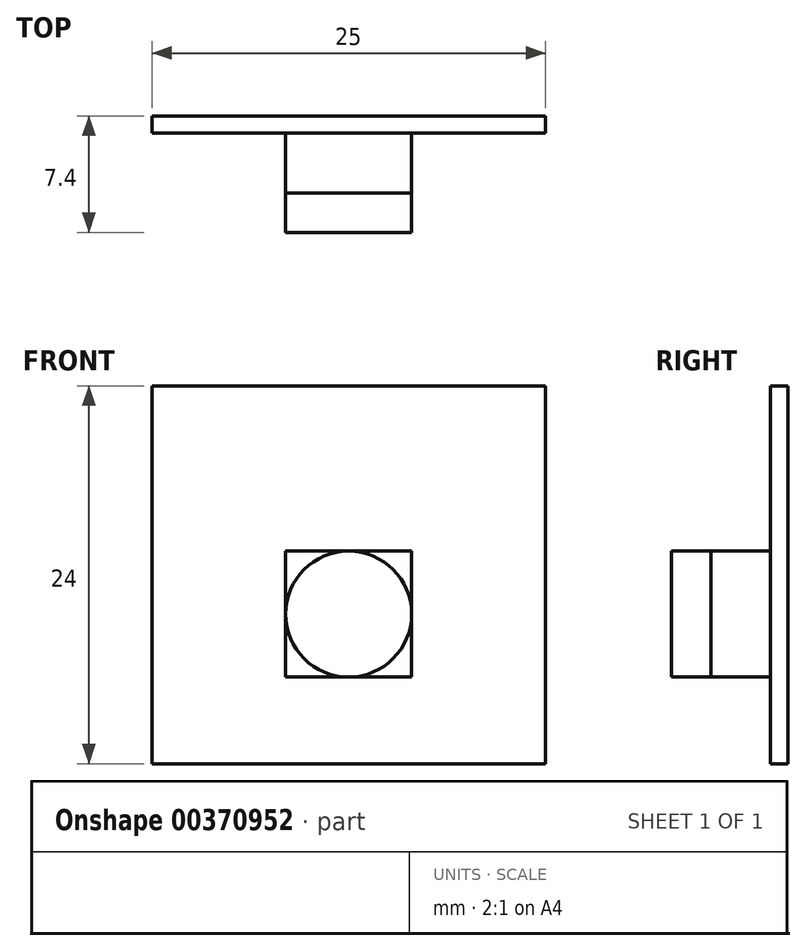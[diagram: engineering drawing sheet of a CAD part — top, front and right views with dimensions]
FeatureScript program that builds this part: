
annotation { "Feature Type Name" : "Feature", "Feature Type Description" : "" }
export const myFeature = defineFeature(function(context is Context, id is Id, definition is map)
    precondition{}
    {
        {
            var Q0;
            Q0=qCreatedBy(makeId("Front.planeOp"),FACE);
            var sketch = newSketch(context, id + "F0", { "sketchPlane" : qUnion([Q0])});
            skLineSegment(sketch, "E0.bottom", {"start": v(0, 0) * mm, "end": v(25, 0) * mm});
            skLineSegment(sketch, "E0.top", {"start": v(0, -24) * mm, "end": v(25, -24) * mm});
            skLineSegment(sketch, "E0.left", {"start": v(0, 0) * mm, "end": v(0, -24) * mm});
            skLineSegment(sketch, "E0.right", {"start": v(25, 0) * mm, "end": v(25, -24) * mm});
            skSolve(sketch);
        }
        {
            var Q0;
            Q0 = qSketchRegion(id + "F0", true);
            extrude(context, id + "F1", {"entities" : qUnion([Q0]), "depth" : 1.1 * mm, "offsetDistance" : 25 * mm});
        }
        {
            var Q0;
            Q0=makeQuery(id+"F1.opExtrude","CAP_FACE",FACE,{"disambiguationData":[OSD([sQuery(id+"F0.wireOp",EDGE,"E0.bottom"),sQuery(id+"F0.wireOp",EDGE,"E0.top"),sQuery(id+"F0.wireOp",EDGE,"E0.left"),sQuery(id+"F0.wireOp",EDGE,"E0.right")])],"isStart":false});
            var sketch = newSketch(context, id + "F2", { "sketchPlane" : qUnion([Q0])});
            skLineSegment(sketch, "E1.bottom", {"start": v(8.5, -10.5) * mm, "end": v(16.5, -10.5) * mm});
            skLineSegment(sketch, "E1.top", {"start": v(8.5, -18.5) * mm, "end": v(16.5, -18.5) * mm});
            skLineSegment(sketch, "E1.left", {"start": v(8.5, -10.5) * mm, "end": v(8.5, -18.5) * mm});
            skLineSegment(sketch, "E1.right", {"start": v(16.5, -10.5) * mm, "end": v(16.5, -18.5) * mm});
            skPoint(sketch, "E2.first.point", {"position": v(12.5, -18.5) * mm});
            skPoint(sketch, "E2.second.point", {"position": v(8.5, -14.5) * mm});
            skPoint(sketch, "E2.third.point", {"position": v(12.5, -10.5) * mm});
            skSolve(sketch);
        }
        {
            var Q0;
            Q0 = qSketchRegion(id + "F2", true);
            extrude(context, id + "F3", {"entities" : qUnion([Q0]), "operationType" : NewBodyOperationType.ADD, "depth" : 3.8 * mm, "offsetDistance" : 25 * mm});
        }
        {
            var Q0;
            Q0=makeQuery(id+"F3.opExtrude","CAP_FACE",FACE,{"disambiguationData":[OSD([sQuery(id+"F2.wireOp",EDGE,"E1.bottom"),sQuery(id+"F2.wireOp",EDGE,"E1.top"),sQuery(id+"F2.wireOp",EDGE,"E1.left"),sQuery(id+"F2.wireOp",EDGE,"E1.right")])],"isStart":false});
            var sketch = newSketch(context, id + "F4", { "sketchPlane" : qUnion([Q0])});
            skCircle(sketch, "E3", {"center": v(12.5, -14.5) * mm, "radius": 4 * mm});
            skPoint(sketch, "E3.first.point", {"position": v(12.5, -18.5) * mm});
            skPoint(sketch, "E3.second.point", {"position": v(8.5, -14.5) * mm});
            skPoint(sketch, "E3.third.point", {"position": v(12.5, -10.5) * mm});
            skSolve(sketch);
        }
        {
            var Q0;
            Q0 = qSketchRegion(id + "F4", true);
            extrude(context, id + "F5", {"entities" : qUnion([Q0]), "operationType" : NewBodyOperationType.ADD, "depth" : 2.5 * mm, "offsetDistance" : 25 * mm});
        }
    });
